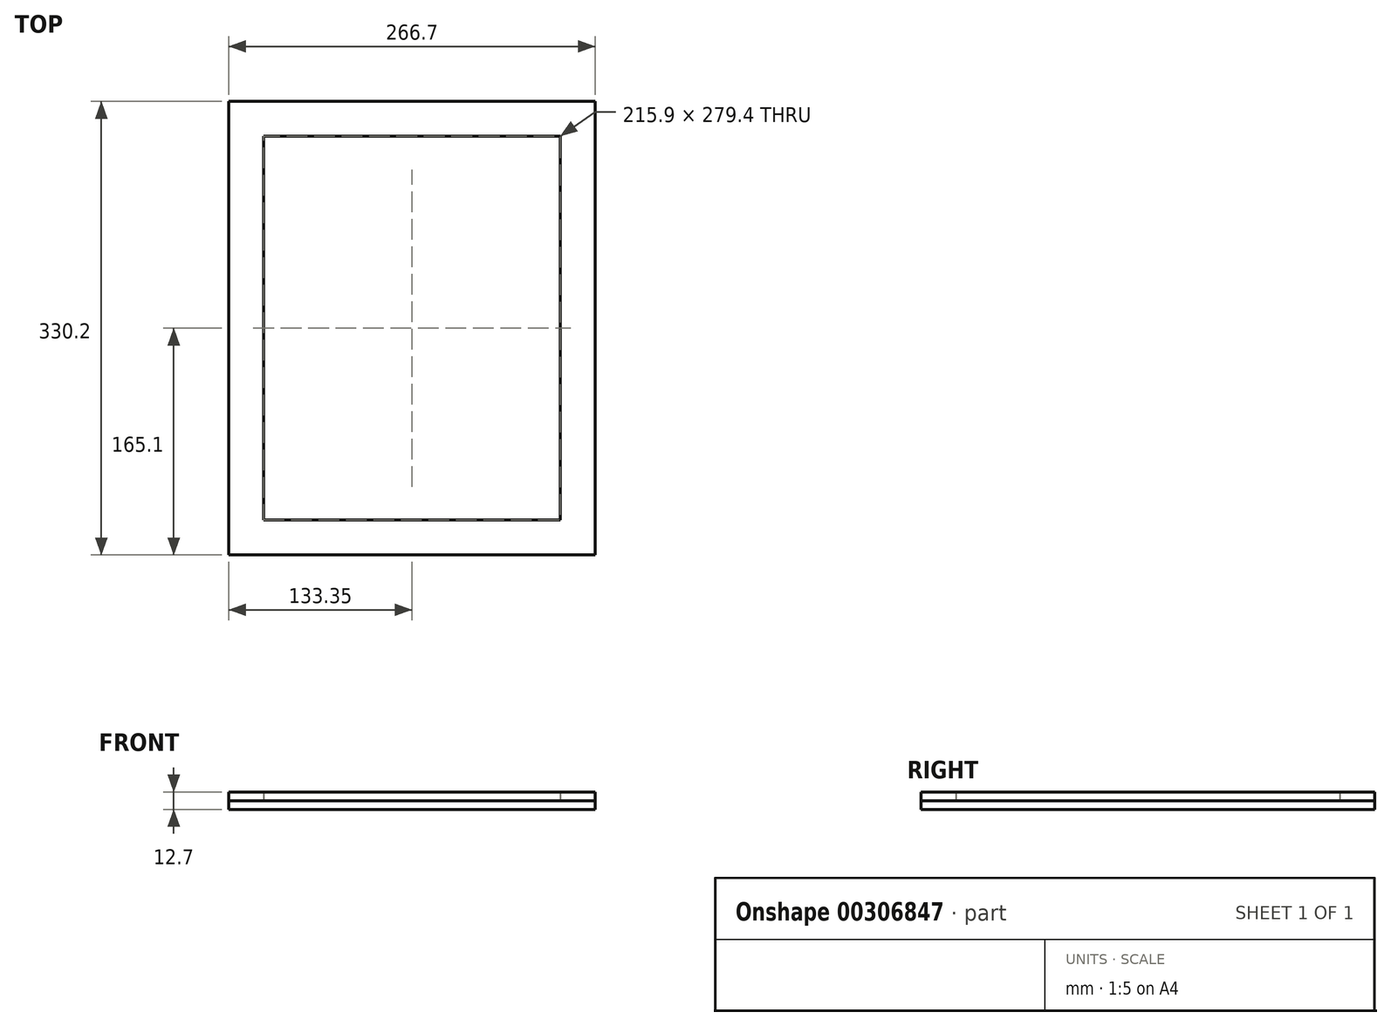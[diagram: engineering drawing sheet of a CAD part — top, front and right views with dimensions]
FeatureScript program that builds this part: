
annotation { "Feature Type Name" : "Feature", "Feature Type Description" : "" }
export const myFeature = defineFeature(function(context is Context, id is Id, definition is map)
    precondition{}
    {
        {
            var Q0;
            Q0=qCreatedBy(makeId("Top.planeOp"),FACE);
            var sketch = newSketch(context, id + "F0", { "sketchPlane" : qUnion([Q0])});
            skLineSegment(sketch, "E0.bottom", {"start": v(0, 279.4) * mm, "end": v(215.9, 279.4) * mm});
            skLineSegment(sketch, "E0.top", {"start": v(0, 0) * mm, "end": v(215.9, 0) * mm});
            skLineSegment(sketch, "E0.left", {"start": v(0, 279.4) * mm, "end": v(0, 0) * mm});
            skLineSegment(sketch, "E0.right", {"start": v(215.9, 279.4) * mm, "end": v(215.9, 0) * mm});
            skLineSegment(sketch, "E1.bottom", {"start": v(-25.4, -25.4) * mm, "end": v(241.3, -25.4) * mm});
            skLineSegment(sketch, "E1.top", {"start": v(-25.4, 304.8) * mm, "end": v(241.3, 304.8) * mm});
            skLineSegment(sketch, "E1.left", {"start": v(-25.4, -25.4) * mm, "end": v(-25.4, 304.8) * mm});
            skLineSegment(sketch, "E1.right", {"start": v(241.3, -25.4) * mm, "end": v(241.3, 304.8) * mm});
            skSolve(sketch);
        }
        {
            var Q0;
            Q0=makeQuery(id+"F0.imprint","IMPRINT",FACE,{"disambiguationData":[TD([[makeQuery(id+"F0.imprint","IMPRINT",EDGE,{"derivedFrom":sQuery(id+"F0.wireOp",EDGE,"E0.bottom")}),1.0]])]});
            var Q1;
            Q1=makeQuery(id+"F0.imprint","IMPRINT",FACE,{"disambiguationData":[TD([[makeQuery(id+"F0.imprint","IMPRINT",EDGE,{"derivedFrom":sQuery(id+"F0.wireOp",EDGE,"E0.bottom")}),-1.0]])]});
            extrude(context, id + "F1", {"entities" : qUnion([Q0, Q1]), "oppositeDirection" : true, "depth" : 6.35 * mm});
        }
        {
            var Q0;
            Q0 = qSketchRegion(id + "F0", true);
            extrude(context, id + "F2", {"entities" : qUnion([Q0]), "depth" : 6.35 * mm});
        }
    });
